# Revit family: Котел газовый настенный_Eco Light_FedericaBugatti_R20
name_source: partatom
category: Оборудование
units: mm (PartAtom-declared; Revit-internal decimal feet)

## family parameters
Всегда вертикально = Да
Классификация = Нет
На основе рабочей плоскости = Нет
Общий = Нет
При загрузке вырезать с полостями = Нет
Размер круглого соединителя = Использовать диаметр
Тип детали = Нормальный
Точка расчета площади = Да

## types (6) — shared parameters
ADSK_Единица измерения = шт
ADSK_Завод-изготовитель = Federica Bugatti
ADSK_Классификация нагрузок = Прочее
ADSK_Количество = 1
ADSK_Количество фаз = 1
ADSK_Коэффициент мощности = 1
ADSK_Напряжение = 230 В
L2 = 65 мм
L5 = 75 мм
Материал_ВнешняяСтенка = RAL 9010 Белый
Материал_Дисплей = ADSK_Полимеры_Пластик черный
Материал_Дисплей_Контур = ADSK_Полимеры_Пластик белый
Материал_Дымоход = ADSK_Металл_Окрашенный_Черный темный
Материал_Корпус = ADSK_Металл_Сталь оцинкованная
Материал_Крепление_Настенное = ADSK_Металл_Сталь нержавеющая
Материал_Патрубки = ADSK_Металл_Сталь оцинкованная
Патрубки_Высота = 10 мм
zero-valued in all types: Отметка по умолчанию

## per-type parameters (varying)
| type | ADSK_Марка | ADSK_Масса | ADSK_Масса_Текст | ADSK_Наименование | ADSK_Номинальная мощность | ADSK_Полная мощность | ADSK_Размер_Высота | ADSK_Размер_Глубина | ADSK_Размер_Ширина | L1 | L10 | L11 | L12 | L3 | L4 | L6 | L8 | Дымоход_Высота2 | ПанельУправления_Толщина |
| EcoLightДвухконтурный_12 | Eco Light 12кВт | 26 | 26 | Котел газовый настенный двухконтурный Eco Light 12кВт | 12000 Вт | 12000 В·А | 700 мм | 403 мм | 265 мм | 48 мм | 200 мм | 75 мм | 100 мм | 65 мм | 55 мм | 95 мм | 255 мм | 0 мм | 10 мм |
| EcoLightДвухконтурный_18 | Eco Light 18кВт | 29 | 29 | Котел газовый настенный двухконтурный Eco Light 18кВт | 18000 Вт | 18000 В·А | 700 мм | 403 мм | 265 мм | 48 мм | 200 мм | 75 мм | 100 мм | 65 мм | 55 мм | 95 мм | 255 мм | 0 мм | 10 мм |
| EcoLightДвухконтурный_24 | Eco Light 24кВт | 29 | 29 | Котел газовый настенный двухконтурный Eco Light 24кВт | 24000 Вт | 24000 В·А | 700 мм | 403 мм | 265 мм | 48 мм | 200 мм | 75 мм | 100 мм | 65 мм | 55 мм | 95 мм | 255 мм | 0 мм | 10 мм |
| EcoLightДвухконтурный_32 | Eco Light 32кВт | 33 | 33 | Котел газовый настенный двухконтурный Eco Light 32кВт | 32000 Вт | 32000 В·А | 725 мм | 450 мм | 350 мм | 127 мм | 226 мм | 137 мм | 145 мм | 61 мм | 59 мм | 63 мм | 344 мм | 5 мм | 6 мм |
| EcoLightОдноконтурный_24 | Eco Light 24кВт | 29 | 29 | Котел газовый настенный одноконтурный Eco Light 24кВт | 24000 Вт | 24000 В·А | 700 мм | 403 мм | 265 мм | 48 мм | 200 мм | 75 мм | 100 мм | 65 мм | 55 мм | 95 мм | 255 мм | 0 мм | 10 мм |
| EcoLightОдноконтурный_32 | Eco Light 32кВт | 33 | 33 | Котел газовый настенный одноконтурный Eco Light 32кВт | 32000 Вт | 32000 В·А | 725 мм | 450 мм | 350 мм | 127 мм | 226 мм | 137 мм | 145 мм | 61 мм | 59 мм | 63 мм | 344 мм | 5 мм | 6 мм |
